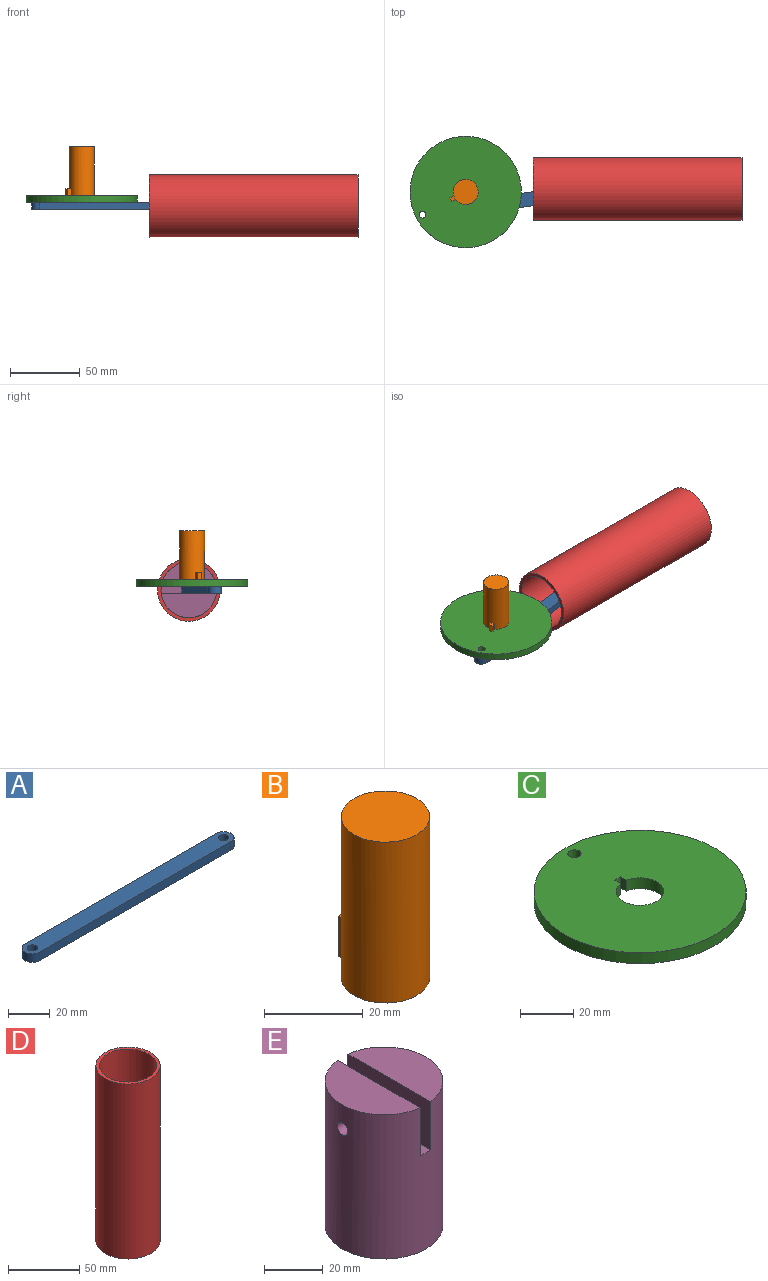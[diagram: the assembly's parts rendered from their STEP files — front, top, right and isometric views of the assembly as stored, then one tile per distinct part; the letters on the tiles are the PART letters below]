
ASSEMBLY  parts=5 mates=5
PART A: 8 faces, bbox 140x10x5 mm
  f0: plane 130x5mm, normal (0,1,0), area 650mm2, adj f1,f5,f6,f7
  f1: cylinder r=5mm len=10mm, axis (0,0,-1), area 78.5mm2, adj f0,f2,f6,f7
  f2: plane 130x5mm, normal (0,-1,0), area 650mm2, adj f1,f5,f6,f7
  f3: cylinder r=2.5mm len=5mm, axis (0,0,-1), area 78.5mm2, adj f6,f7
  f4: cylinder r=2.5mm len=5mm, axis (0,0,-1), area 78.5mm2, adj f6,f7
  f5: cylinder r=5mm len=10mm, axis (0,0,-1), area 78.5mm2, adj f0,f2,f6,f7
  f6: plane 140x10mm, normal (0,0,1), area 1339.3mm2, adj f0,f1,f2,f3,f4,f5
  f7: plane 140x10mm, normal (0,0,-1), area 1339.3mm2, adj f0,f1,f2,f3,f4,f5
PART B: 7 faces, bbox 18x21x40 mm
  f0: plane 10x3.13mm, normal (-1,0,0), area 31.3mm2, adj f2,f4,f5,f6
  f1: plane 10x3.13mm, normal (1,0,0), area 31.3mm2, adj f2,f4,f5,f6
  f2: plane 10x3mm, normal (0,1,0), area 30mm2, adj f0,f1,f5,f6
  f3: plane 18x18mm, normal (0,0,1), area 254.5mm2, adj f4
  f4: cylinder r=9mm len=40mm, axis (0,0,-1), area 2231.8mm2, adj f0,f1,f3,f5,f6
  f5: plane 21x18mm, normal (0,0,-1), area 263.6mm2, adj f0,f1,f2,f4
  f6: plane 3.13x3mm, normal (0,0,1), area 9.1mm2, adj f0,f1,f2,f4
PART C: 8 faces, bbox 80x80x5 mm
  f0: cylinder r=9mm len=18mm, axis (0,0,-1), area 267.7mm2, adj f1,f2,f5,f7
  f1: plane 80x80mm, normal (0,0,1), area 4743.3mm2, adj f0,f3,f4,f5,f6,f7
  f2: plane 80x80mm, normal (0,0,-1), area 4743.3mm2, adj f0,f3,f4,f5,f6,f7
  f3: cylinder r=2.5mm len=5mm, axis (0,0,-1), area 78.5mm2, adj f1,f2
  f4: cylinder r=40mm len=80mm, axis (0,0,-1), area 1256.6mm2, adj f1,f2
  f5: plane 5x3.13mm, normal (-1,0,0), area 15.6mm2, adj f0,f1,f2,f6
  f6: plane 5x3mm, normal (0,-1,0), area 15mm2, adj f1,f2,f5,f7
  f7: plane 5x3.13mm, normal (1,0,0), area 15.6mm2, adj f0,f1,f2,f6
PART D: 4 faces, bbox 45x45x150 mm
  f0: cylinder r=20mm len=150mm, axis (0,0,-1), area 18849.6mm2, adj f2,f3
  f1: cylinder r=22.5mm len=150mm, axis (0,0,-1), area 21205.8mm2, adj f2,f3
  f2: plane 45x45mm, normal (0,0,1), area 333.8mm2, adj f0,f1
  f3: plane 45x45mm, normal (0,0,-1), area 333.8mm2, adj f0,f1
PART E: 9 faces, bbox 40x40x60 mm
  f0: cylinder r=20mm len=60mm, axis (0,0,-1), area 7300mm2, adj f1,f2,f3,f4,f5,f6,f7,f8
  f1: plane 39.69x17.5mm, normal (0,0,1), area 528.6mm2, adj f0,f4
  f2: plane 39.69x17.5mm, normal (0,0,1), area 528.6mm2, adj f0,f5
  f3: plane 40x40mm, normal (0,0,-1), area 1256.6mm2, adj f0
  f4: plane 39.69x20mm, normal (-1,0,0), area 774.1mm2, adj f0,f1,f6,f8
  f5: plane 39.69x20mm, normal (1,0,0), area 774.1mm2, adj f0,f2,f6,f7
  f6: plane 40x5mm, normal (0,0,1), area 199.5mm2, adj f0,f4,f5
  f7: cylinder r=2.5mm len=17.5mm, axis (1,0,0), area 273.7mm2, adj f0,f5
  f8: cylinder r=2.5mm len=17.5mm, axis (1,0,0), area 273.7mm2, adj f0,f4
PLACE A rot(axis=(-1,-0.07,0),180deg) t=(7.55,52.09,-116.28)mm
PLACE B rot(axis=(0,0,1),117.6deg) t=(112.58,-21.2,-116.28)mm
PLACE C rot(axis=(0,0,1),117.6deg) t=(122.57,67.43,-116.28)mm
PLACE D rot(axis=(0,-1,0),90deg) t=(272.21,-166.88,-101.08)mm fixed
PLACE E rot(axis=(0.71,0,-0.71),180deg) t=(221.37,138.49,-55.26)mm
MATE revolute A.f1 <-> C.f3  axis (0,0,1) through (42.7,-6.46,-116.28)mm
MATE revolute E.f7 <-> A.f4  axis (0,0,1) through (171.37,12.04,-121.28)mm
MATE planar B.f4 <-> C.f2  axis (0,0,-1) through (73.72,9.74,-116.28)mm
MATE slider B.f4 <-> C.f0  axis (0,0,-1) through (73.72,9.74,-116.28)mm
MATE slider D.f0 <-> E.f0  axis (1,0,0) through (122.21,12.04,-118.78)mm
